FREECAD ASSEMBLY — COMPONENT RECIPES ("enclousre")

This assembly document has 2 components, labeled P0..P1 below (a component is one placed body or linked part). 1 of them carries a construction recipe — the FreeCAD feature program that regenerates the part from scratch, quoted from this document or its linked companion documents; the rest are supplied as boundary geometry only. No exploded tour is included for this assembly.
COMPONENT P0 — geometry summary ("PCB"; no construction recipe available for this part):
  bounding box: 160.8 x 55.7 x 32.7 mm
  tessellated surface: 548,648 triangles
  volume: 6076 mm^3 (2% of its bounding box)
COMPONENT P1 — recipe-attached ("Case", modeled in this document).
Construction recipe (the document's own serialized feature program — sketch geometry with constraints, then the solid features built on it; lengths are millimeters unless a unit is written):

FEATURE [Sketcher::SketchObject] Sketch
  FullyConstrained = true
  MapMode = 5
  Support = -> [XY_Plane011]
  expr: Constraints[8] = Spreadsheet.wall_thickness * 2 + Spreadsheet.pcb_clearance * 2 + Spreadsheet.pcb_length
  expr: Constraints[9] = Spreadsheet.wall_thickness * 2 + Spreadsheet.pcb_clearance * 2 + Spreadsheet.pcb_width
  sketch-geometry (4):
    g0: LineSegment StartX=0 StartY=59.308 StartZ=0 EndX=168.782 EndY=59.308 EndZ=0
    g1: LineSegment StartX=168.782 StartY=59.308 StartZ=0 EndX=168.782 EndY=0 EndZ=0
    g2: LineSegment StartX=168.782 StartY=0 StartZ=0 EndX=0 EndY=0 EndZ=0
    g3: LineSegment StartX=0 StartY=0 StartZ=0 EndX=0 EndY=59.308 EndZ=0
  constraints (11):
    c: Coincident(g0,g1)
    c: Coincident(g1,g2)
    c: Coincident(g2,g3)
    c: Coincident(g3,g0)
    c: Horizontal(g0)
    c: Horizontal(g2)
    c: Vertical(g1)
    c: Vertical(g3)
    c: DistanceX(g0,g0) = 168.782
    c: DistanceY(g1,g1) = 59.308
    c: Coincident(g2,g-1)
FEATURE [PartDesign::Pad] Pad
  Direction = (0,0,1)
  Length = 40
  Length2 = 10
  Profile = -> Sketch
  ReferenceAxis = -> Sketch [N_Axis]
  Type = 0
FEATURE [PartDesign::Body] Body  label="exterior case"
  Group = -> [Sketch,Pad]
  Origin = -> Origin011
  Tip = -> Pad
FEATURE [Sketcher::SketchObject] Sketch001
  FullyConstrained = false
  MapMode = 5
  Support = -> [XY_Plane012]
  expr: Constraints[8] = Spreadsheet.usb_width
  expr: Constraints[9] = Spreadsheet.usb_depth + Spreadsheet.usb_extend_in + Spreadsheet.usb_extend_out
  sketch-geometry (4):
    g0: LineSegment StartX=141.084 StartY=58.1464 StartZ=0 EndX=148.884 EndY=58.1464 EndZ=0
    g1: LineSegment StartX=148.884 StartY=58.1464 StartZ=0 EndX=148.884 EndY=50.1464 EndZ=0
    g2: LineSegment StartX=148.884 StartY=50.1464 StartZ=0 EndX=141.084 EndY=50.1464 EndZ=0
    g3: LineSegment StartX=141.084 StartY=50.1464 StartZ=0 EndX=141.084 EndY=58.1464 EndZ=0
  constraints (10):
    c: Coincident(g0,g1)
    c: Coincident(g1,g2)
    c: Coincident(g2,g3)
    c: Coincident(g3,g0)
    c: Horizontal(g0)
    c: Horizontal(g2)
    c: Vertical(g1)
    c: Vertical(g3)
    c: DistanceX(g0,g0) = 7.8
    c: DistanceY(g1,g1) = 8
FEATURE [PartDesign::Body] Body001  label="usb port hole"
  Group = -> [Sketch001]
  Origin = -> Origin012
PROVENANCE & LICENSES
A FreeCAD (.FCStd) document from a public repository crawl; recipes are the document's own serialized feature recipes (and, for linked parts, companion documents' recipes).
License: as declared in the source repository (recorded in the dataset sidecar).
